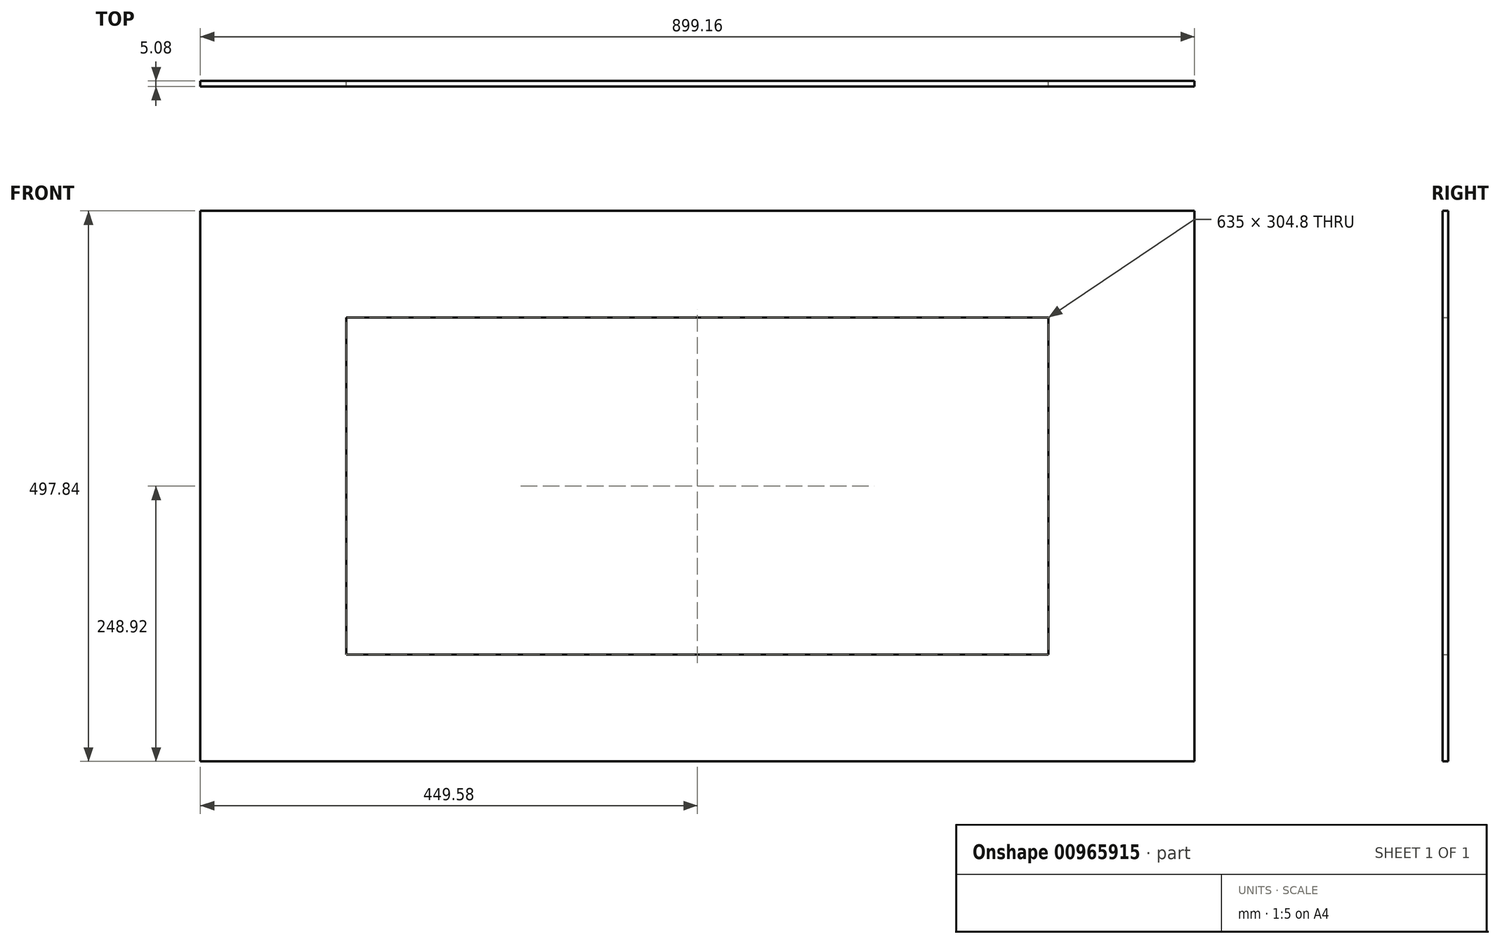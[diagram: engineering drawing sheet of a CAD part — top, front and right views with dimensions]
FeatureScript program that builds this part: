
annotation { "Feature Type Name" : "Feature", "Feature Type Description" : "" }
export const myFeature = defineFeature(function(context is Context, id is Id, definition is map)
    precondition{}
    {
        {
            var Q0;
            Q0=qCreatedBy(makeId("Front.planeOp"),FACE);
            var sketch = newSketch(context, id + "F0", { "sketchPlane" : qUnion([Q0])});
            skLineSegment(sketch, "E0.bottom", {"start": v(0, 0) * mm, "end": v(899.16, 0) * mm});
            skLineSegment(sketch, "E0.top", {"start": v(0, -497.84) * mm, "end": v(899.16, -497.84) * mm});
            skLineSegment(sketch, "E0.left", {"start": v(0, 0) * mm, "end": v(0, -497.84) * mm});
            skLineSegment(sketch, "E0.right", {"start": v(899.16, 0) * mm, "end": v(899.16, -497.84) * mm});
            skLineSegment(sketch, "E1.bottom", {"start": v(132.08, -96.52) * mm, "end": v(767.08, -96.52) * mm});
            skLineSegment(sketch, "E1.top", {"start": v(132.08, -401.32) * mm, "end": v(767.08, -401.32) * mm});
            skLineSegment(sketch, "E1.left", {"start": v(132.08, -96.52) * mm, "end": v(132.08, -401.32) * mm});
            skLineSegment(sketch, "E1.right", {"start": v(767.08, -96.52) * mm, "end": v(767.08, -401.32) * mm});
            skSolve(sketch);
        }
        {
            var Q0;
            Q0=makeQuery(id+"F0.imprint","IMPRINT",FACE,{"disambiguationData":[TD([[makeQuery(id+"F0.imprint","IMPRINT",EDGE,{"derivedFrom":sQuery(id+"F0.wireOp",EDGE,"E0.bottom")}),-1.0]])]});
            extrude(context, id + "F1", {"entities" : qUnion([Q0]), "depth" : 5.08 * mm, "offsetDistance" : 25.4 * mm});
        }
    });
